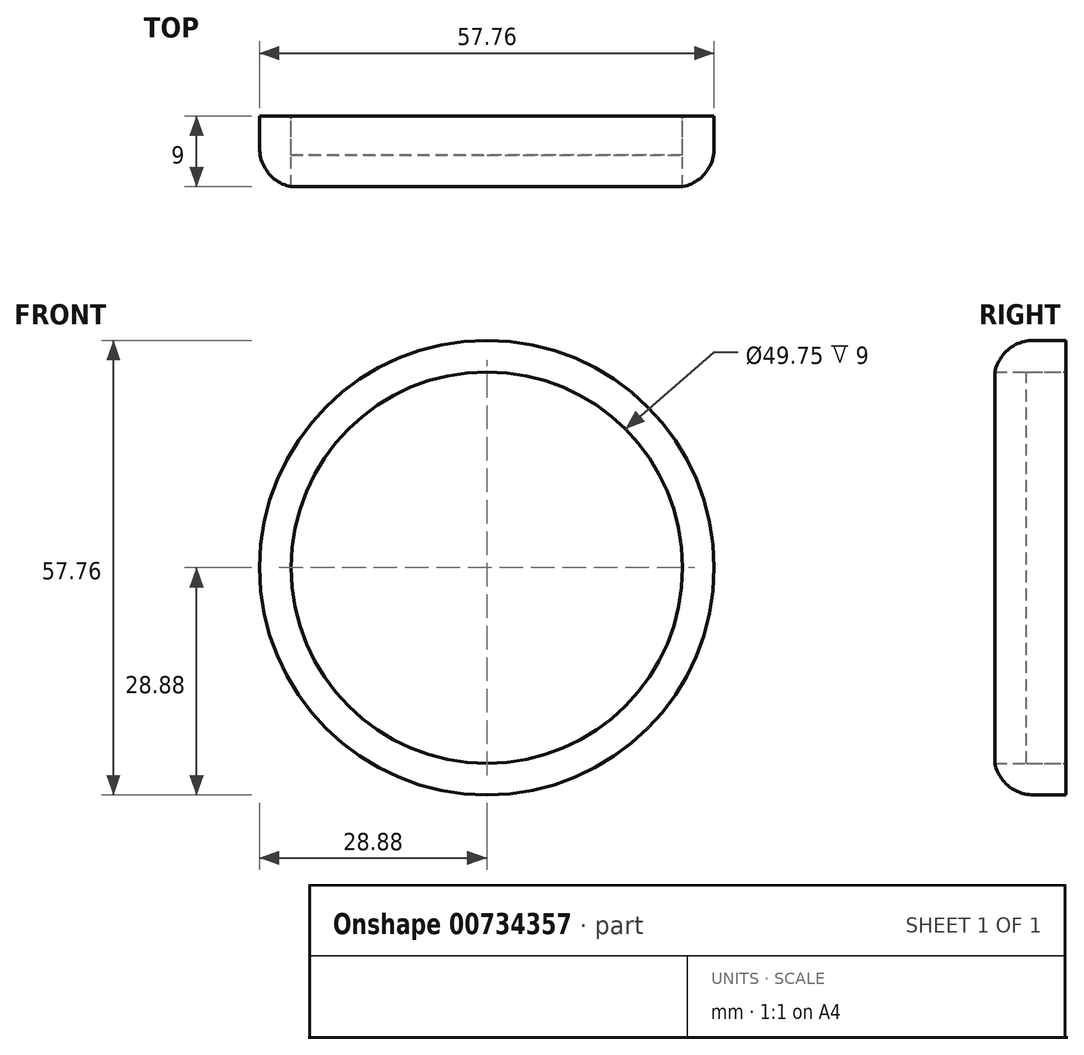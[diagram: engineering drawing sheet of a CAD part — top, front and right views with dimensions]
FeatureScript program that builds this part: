
annotation { "Feature Type Name" : "Feature", "Feature Type Description" : "" }
export const myFeature = defineFeature(function(context is Context, id is Id, definition is map)
    precondition{}
    {
        {
            var Q0;
            Q0=qCreatedBy(makeId("Front.planeOp"),FACE);
            var sketch = newSketch(context, id + "F0", { "sketchPlane" : qUnion([Q0])});
            skCircle(sketch, "E0", {"center": v(0, 0) * mm, "radius": 24.88 * mm});
            skCircle(sketch, "E1", {"center": v(0, 0) * mm, "radius": 28.88 * mm});
            skSolve(sketch);
        }
        {
            var Q0;
            Q0=makeQuery(id+"F0.imprint","IMPRINT",FACE,{"disambiguationData":[TD([[makeQuery(id+"F0.imprint","IMPRINT",EDGE,{"derivedFrom":sQuery(id+"F0.wireOp",EDGE,"E0")}),1.0]])]});
            var Q1;
            Q1=sQuery(id+"F0.wireOp",EDGE,"E0");
            extrude(context, id + "F1", {"entities" : qUnion([Q0]), "surfaceEntities" : qUnion([Q1]), "depth" : 5 * mm, "offsetDistance" : 25 * mm});
        }
        {
            var Q0;
            Q0=makeQuery(id+"F0.imprint","IMPRINT",FACE,{"disambiguationData":[TD([[makeQuery(id+"F0.imprint","IMPRINT",EDGE,{"derivedFrom":sQuery(id+"F0.wireOp",EDGE,"E0")}),-1.0]])]});
            extrude(context, id + "F2", {"entities" : qUnion([Q0]), "depth" : 9 * mm, "offsetDistance" : 25 * mm});
        }
        {
            var Q0;
            Q0=makeQuery(id+"F2.opExtrude","CAP_EDGE",EDGE,{"disambiguationData":[OSD([sQuery(id+"F0.wireOp",EDGE,"E1")])],"isStart":false});
            fillet(context, id + "F3", {"entities" : qUnion([Q0]), "radius" : 5 * mm, "tangentPropagation" : true, "allowEdgeOverflow" : false});
        }
    });
